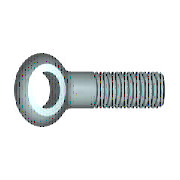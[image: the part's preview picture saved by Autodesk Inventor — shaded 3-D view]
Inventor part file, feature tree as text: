
AUTODESK INVENTOR PART (.ipt)
format: ipt  version: 2018 (Build 220112000, 112)  size: 174,080 bytes
history: native  units: mm (DEFAULTED — no unit token found)
features: other x2, sketch x2, extrude x1, hole x1
ambient origin geometry x8: Origin, YZ Plane, XZ Plane, XY Plane, X Axis, Y Axis, Z Axis, Center Point
bodies: Solid1 (feature_tree)
feature tree (6):
  other  "Corpo1"
  other  "IDS_WORKPLANE{1}"
  extrude  "Corpo2"  Depth=6.0mm
  hole  "Occhiello"  [1 undecoded]
  sketch  "Schizzo1"
  sketch  "Schizzo3"
note: 1 required parameter value undecoded (feature->parameter linkage not recoverable at this tier; creation-order binding heuristic only, values carry confidence <= 0.55)
